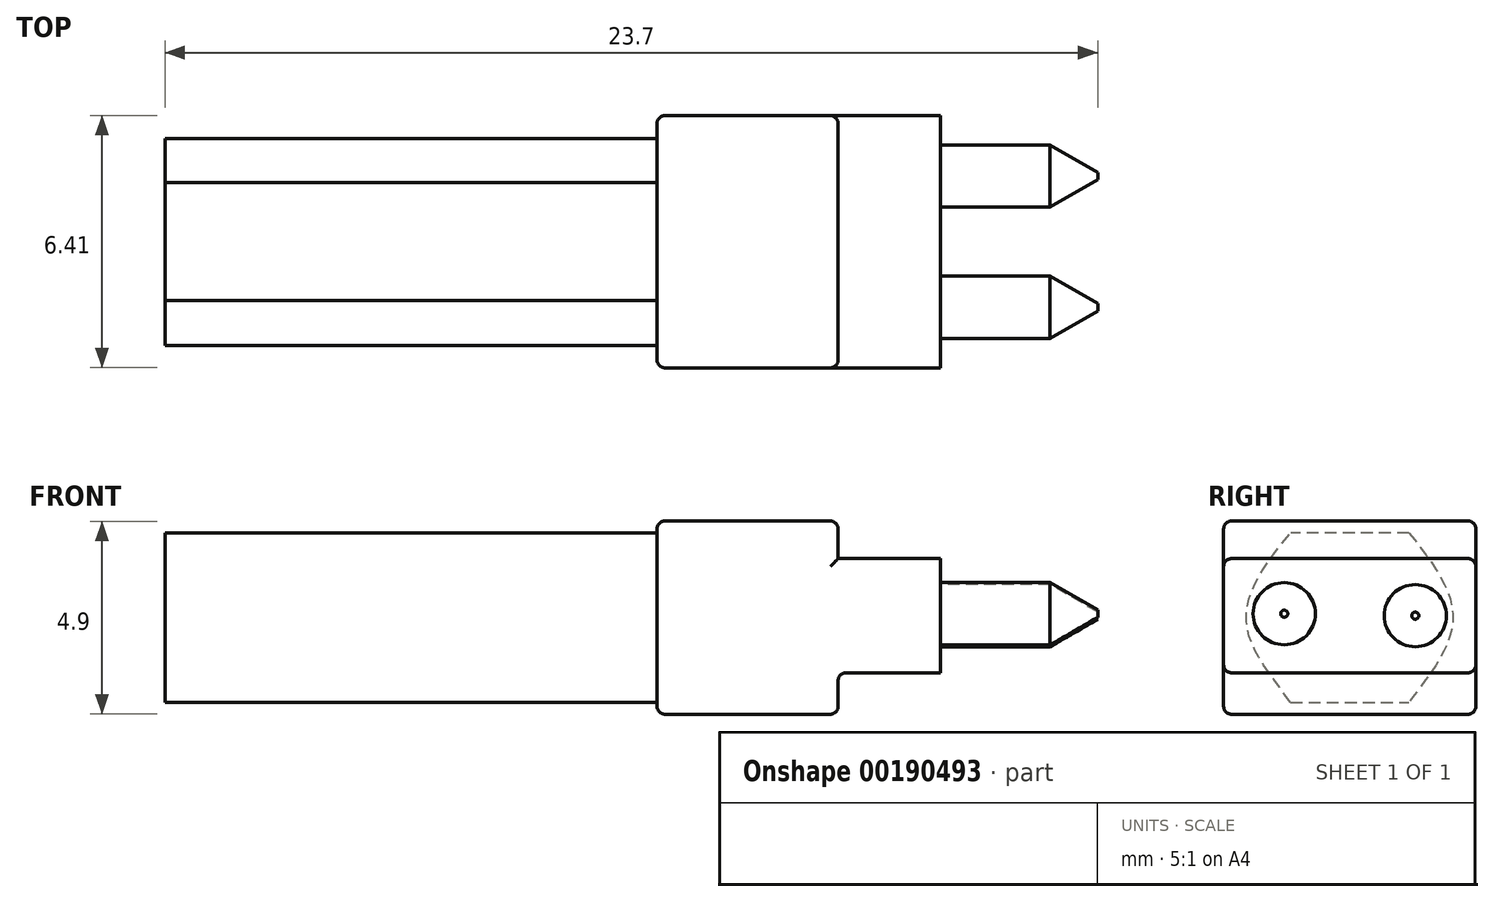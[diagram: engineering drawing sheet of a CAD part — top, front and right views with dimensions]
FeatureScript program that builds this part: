
annotation { "Feature Type Name" : "Feature", "Feature Type Description" : "" }
export const myFeature = defineFeature(function(context is Context, id is Id, definition is map)
    precondition{}
    {
        {
            var Q0;
            Q0=qCreatedBy(makeId("Top.planeOp"),FACE);
            var sketch = newSketch(context, id + "F0", { "sketchPlane" : qUnion([Q0])});
            skLineSegment(sketch, "E0.bottom", {"start": v(-2.48, 2.08) * mm, "end": v(4.72, 2.08) * mm});
            skLineSegment(sketch, "E0.top", {"start": v(-2.48, -4.33) * mm, "end": v(4.72, -4.33) * mm});
            skLineSegment(sketch, "E0.left", {"start": v(-2.48, 2.08) * mm, "end": v(-2.48, -4.33) * mm});
            skLineSegment(sketch, "E0.right", {"start": v(4.72, 2.08) * mm, "end": v(4.72, -4.33) * mm});
            skSolve(sketch);
        }
        {
            var Q0;
            Q0=makeQuery(id+"F0.imprint","IMPRINT",FACE,{"disambiguationData":[TD([[makeQuery(id+"F0.imprint","IMPRINT",EDGE,{"derivedFrom":sQuery(id+"F0.wireOp",EDGE,"E0.bottom")}),-1.0]])]});
            var sketch = newSketch(context, id + "F1", { "sketchPlane" : qUnion([Q0])});
            skSolve(sketch);
        }
        {
            var Q0;
            Q0=makeQuery(id+"F1.imprint","IMPRINT",FACE,{"disambiguationData":[TD([[makeQuery(id+"F1.imprint","IMPRINT",EDGE,{"derivedFrom":makeQuery(id+"F0.imprint","IMPRINT",EDGE,{"derivedFrom":sQuery(id+"F0.wireOp",EDGE,"E0.bottom")})}),-1.0]])]});
            extrude(context, id + "F2", {"entities" : qUnion([Q0]), "depth" : 2.9 * mm, "offsetDistance" : 25 * mm});
        }
        {
            var Q0;
            Q0=makeQuery(id+"F2.opExtrude","CAP_FACE",FACE,{"disambiguationData":[OSD([sQuery(id+"F0.wireOp",EDGE,"E0.bottom"),sQuery(id+"F0.wireOp",EDGE,"E0.top"),sQuery(id+"F0.wireOp",EDGE,"E0.left"),sQuery(id+"F0.wireOp",EDGE,"E0.right")])],"isStart":false});
            var sketch = newSketch(context, id + "F3", { "sketchPlane" : qUnion([Q0])});
            skLineSegment(sketch, "E1.bottom", {"start": v(-2.48, 2.08) * mm, "end": v(2.12, 2.08) * mm});
            skLineSegment(sketch, "E1.top", {"start": v(-2.48, -4.33) * mm, "end": v(2.12, -4.33) * mm});
            skLineSegment(sketch, "E1.left", {"start": v(-2.48, 2.08) * mm, "end": v(-2.48, -4.33) * mm});
            skLineSegment(sketch, "E1.right", {"start": v(2.12, 2.08) * mm, "end": v(2.12, -4.33) * mm});
            skSolve(sketch);
        }
        {
            var Q0;
            Q0 = qSketchRegion(id + "F3", true);
            extrude(context, id + "F4", {"entities" : qUnion([Q0]), "operationType" : NewBodyOperationType.ADD, "depth" : 0.95 * mm, "offsetDistance" : 25 * mm});
        }
        {
            var Q0;
            Q0 = qSketchRegion(id + "F3", true);
            extrude(context, id + "F5", {"entities" : qUnion([Q0]), "operationType" : NewBodyOperationType.ADD, "oppositeDirection" : true, "depth" : 3.96 * mm, "offsetDistance" : 25 * mm});
        }
        {
            var Q0;
            Q0=makeQuery(id+"F4.opExtrude","CAP_EDGE",EDGE,{"disambiguationData":[OSD([sQuery(id+"F3.wireOp",EDGE,"E1.right")])],"isStart":false});
            var Q1;
            Q1=makeQuery(id+"F4.opExtrude","CAP_EDGE",EDGE,{"disambiguationData":[OSD([sQuery(id+"F3.wireOp",EDGE,"E1.top")])],"isStart":false});
            var Q2;
            Q2=makeQuery(id+"F4.opExtrude","CAP_EDGE",EDGE,{"disambiguationData":[OSD([sQuery(id+"F3.wireOp",EDGE,"E1.left")])],"isStart":false});
            var Q3;
            Q3=makeQuery(id+"F4.opExtrude","CAP_EDGE",EDGE,{"disambiguationData":[OSD([sQuery(id+"F3.wireOp",EDGE,"E1.bottom")])],"isStart":false});
            var Q4;
            Q4=makeQuery(id+"F2.opExtrude","CAP_EDGE",EDGE,{"disambiguationData":[OSD([sQuery(id+"F0.wireOp",EDGE,"E0.top")])],"isStart":false});
            var Q5;
            Q5=makeQuery(id+"F4.opExtrude","SWEPT_EDGE",EDGE,{"disambiguationData":[OSD([sQuery(id+"F0.wireOp",EDGE,"E0.top"),sQuery(id+"F3.wireOp",EDGE,"E1.top"),sQuery(id+"F3.wireOp",EDGE,"E1.right")])]});
            var Q6;
            {var subQ0=sQuery(id+"F3.wireOp",EDGE,"E1.left");var subQ1=sQuery(id+"F3.wireOp",EDGE,"E1.top");Q6=makeQuery(id+"F5.boolean.opBoolean","MERGE",EDGE,{"derivedFrom":[makeQuery(id+"F4.boolean.opBoolean","MERGE",EDGE,{"derivedFrom":[makeQuery(id+"F2.opExtrude","SWEPT_EDGE",EDGE,{"disambiguationData":[OSD([sQuery(id+"F0.wireOp",EDGE,"E0.top"),sQuery(id+"F0.wireOp",EDGE,"E0.left")])]}),makeQuery(id+"F4.opExtrude","SWEPT_EDGE",EDGE,{"disambiguationData":[OSD([subQ1,subQ0])]})]}),makeQuery(id+"F5.opExtrude","SWEPT_EDGE",EDGE,{"disambiguationData":[OSD([subQ1,subQ0])]})]});}
            var Q7;
            Q7=makeQuery(id+"F5.opExtrude","CAP_EDGE",EDGE,{"disambiguationData":[OSD([sQuery(id+"F3.wireOp",EDGE,"E1.top")])],"isStart":false});
            var Q8;
            Q8=makeQuery(id+"F5.opExtrude","CAP_EDGE",EDGE,{"disambiguationData":[OSD([sQuery(id+"F3.wireOp",EDGE,"E1.right")])],"isStart":false});
            var Q9;
            Q9=makeQuery(id+"F5.opExtrude","CAP_EDGE",EDGE,{"disambiguationData":[OSD([sQuery(id+"F3.wireOp",EDGE,"E1.bottom")])],"isStart":false});
            var Q10;
            Q10=makeQuery(id+"F5.opExtrude","SWEPT_EDGE",EDGE,{"disambiguationData":[OSD([sQuery(id+"F0.wireOp",EDGE,"E0.top"),sQuery(id+"F3.wireOp",EDGE,"E1.top"),sQuery(id+"F3.wireOp",EDGE,"E1.right")])]});
            var Q11;
            Q11=makeQuery(id+"F2.opExtrude","CAP_EDGE",EDGE,{"disambiguationData":[OSD([sQuery(id+"F0.wireOp",EDGE,"E0.top")])],"isStart":true});
            var Q12;
            Q12=makeQuery(id+"F5.opExtrude","SWEPT_EDGE",EDGE,{"disambiguationData":[OSD([sQuery(id+"F0.wireOp",EDGE,"E0.bottom"),sQuery(id+"F3.wireOp",EDGE,"E1.bottom"),sQuery(id+"F3.wireOp",EDGE,"E1.right")])]});
            var Q13;
            Q13=makeQuery(id+"F2.opExtrude","CAP_EDGE",EDGE,{"disambiguationData":[OSD([sQuery(id+"F0.wireOp",EDGE,"E0.bottom")])],"isStart":false});
            var Q14;
            Q14=makeQuery(id+"F4.opExtrude","SWEPT_EDGE",EDGE,{"disambiguationData":[OSD([sQuery(id+"F0.wireOp",EDGE,"E0.bottom"),sQuery(id+"F3.wireOp",EDGE,"E1.bottom"),sQuery(id+"F3.wireOp",EDGE,"E1.right")])]});
            var Q15;
            Q15=makeQuery(id+"F2.opExtrude","CAP_EDGE",EDGE,{"disambiguationData":[OSD([sQuery(id+"F0.wireOp",EDGE,"E0.bottom")])],"isStart":true});
            var Q16;
            {var subQ0=sQuery(id+"F3.wireOp",EDGE,"E1.left");var subQ1=sQuery(id+"F3.wireOp",EDGE,"E1.bottom");Q16=makeQuery(id+"F5.boolean.opBoolean","MERGE",EDGE,{"derivedFrom":[makeQuery(id+"F4.boolean.opBoolean","MERGE",EDGE,{"derivedFrom":[makeQuery(id+"F2.opExtrude","SWEPT_EDGE",EDGE,{"disambiguationData":[OSD([sQuery(id+"F0.wireOp",EDGE,"E0.bottom"),sQuery(id+"F0.wireOp",EDGE,"E0.left")])]}),makeQuery(id+"F4.opExtrude","SWEPT_EDGE",EDGE,{"disambiguationData":[OSD([subQ1,subQ0])]})]}),makeQuery(id+"F5.opExtrude","SWEPT_EDGE",EDGE,{"disambiguationData":[OSD([subQ1,subQ0])]})]});}
            var Q17;
            Q17=makeQuery(id+"F5.opExtrude","CAP_EDGE",EDGE,{"disambiguationData":[OSD([sQuery(id+"F3.wireOp",EDGE,"E1.left")])],"isStart":false});
            var Q18;
            Q18=makeQuery(id+"F5.boolean.opBoolean","INTERSECT",EDGE,{"derivedFrom":[makeQuery(id+"F2.opExtrude","CAP_FACE",FACE,{"disambiguationData":[OSD([sQuery(id+"F0.wireOp",EDGE,"E0.bottom"),sQuery(id+"F0.wireOp",EDGE,"E0.top"),sQuery(id+"F0.wireOp",EDGE,"E0.left"),sQuery(id+"F0.wireOp",EDGE,"E0.right")])],"isStart":true}),makeQuery(id+"F5.opExtrude","SWEPT_FACE",FACE,{"disambiguationData":[OSD([sQuery(id+"F3.wireOp",EDGE,"E1.right")])]})]});
            fillet(context, id + "F6", {"entities" : qUnion([Q0, Q1, Q2, Q3, Q4, Q5, Q6, Q7, Q8, Q9, Q10, Q11, Q12, Q13, Q14, Q15, Q16, Q17, Q18]), "tangentPropagation" : true, "radius" : .2 * mm, "defaultsChanged" : false, "vertexSettings" : [], "allowEdgeOverflow" : false});
        }
        {
            var Q0;
            Q0=makeQuery(id+"F2.opExtrude","SWEPT_FACE",FACE,{"disambiguationData":[OSD([sQuery(id+"F0.wireOp",EDGE,"E0.right")])]});
            var sketch = newSketch(context, id + "F7", { "sketchPlane" : qUnion([Q0])});
            skCircle(sketch, "E2", {"center": v(-2.8, 1.5) * mm, "radius": 0.79 * mm});
            skCircle(sketch, "E3", {"center": v(0.54, 1.45) * mm, "radius": 0.79 * mm});
            skSolve(sketch);
        }
        {
            var Q0;
            Q0 = qSketchRegion(id + "F7", true);
            var Q1;
            Q1 = qSketchRegion(id + "FXM3ZPi4sPy6rrn_1", true);
            extrude(context, id + "F8", {"entities" : qUnion([Q0, Q1]), "operationType" : NewBodyOperationType.ADD, "depth" : 4 * mm, "offsetDistance" : 25 * mm});
        }
        {
            var Q0;
            Q0=makeQuery(id+"F8.opExtrude","CAP_FACE",FACE,{"disambiguationData":[OSD([sQuery(id+"F7.wireOp",EDGE,"E2")])],"isStart":false});
            var Q1;
            Q1=makeQuery(id+"F8.opExtrude","CAP_FACE",FACE,{"disambiguationData":[OSD([sQuery(id+"F7.wireOp",EDGE,"E3")])],"isStart":false});
            chamfer(context, id + "F9", {"entities" : qUnion([Q0, Q1]), "chamferType" : ChamferType.OFFSET_ANGLE, "width" : .7 * mm, "oppositeDirection" : false, "angle" : 60 * degree, "tangentPropagation" : true});
        }
        {
            var Q0;
            {var subQ0=sQuery(id+"F3.wireOp",EDGE,"E1.left");Q0=makeQuery(id+"F5.boolean.opBoolean","MERGE",FACE,{"derivedFrom":[makeQuery(id+"F4.boolean.opBoolean","MERGE",FACE,{"derivedFrom":[makeQuery(id+"F2.opExtrude","SWEPT_FACE",FACE,{"disambiguationData":[OSD([sQuery(id+"F0.wireOp",EDGE,"E0.left")])]}),makeQuery(id+"F4.opExtrude","SWEPT_FACE",FACE,{"disambiguationData":[OSD([subQ0])]})]}),makeQuery(id+"F5.opExtrude","SWEPT_FACE",FACE,{"disambiguationData":[OSD([subQ0])]})]});}
            var sketch = newSketch(context, id + "F10", { "sketchPlane" : qUnion([Q0])});
            skLineSegment(sketch, "E4", {"start": v(-0.38, 3.56) * mm, "end": v(2.62, 3.56) * mm});
            skLineSegment(sketch, "E5", {"start": v(2.63, -0.76) * mm, "end": v(-0.37, -0.76) * mm});
            skFitSpline(sketch, "E6", {"points": [v(-0.38, 3.55) * mm, v(-1.5, 1.4) * mm, v(-0.37, -0.76) * mm], "startDerivative": vector(-3.36, -4.25) * mm, "endDerivative": vector(3.37, -4.37) * mm});
            skFitSpline(sketch, "E7", {"points": [v(2.63, -0.76) * mm, v(3.76, 1.4) * mm, v(2.62, 3.56) * mm], "startDerivative": vector(3.34, 4.59) * mm, "endDerivative": vector(-3.42, 4.03) * mm});
            skSolve(sketch);
        }
        {
            var Q0;
            Q0 = qSketchRegion(id + "F10", true);
            extrude(context, id + "F11", {"entities" : qUnion([Q0]), "operationType" : NewBodyOperationType.ADD, "depth" : 12.5 * mm, "offsetDistance" : 25 * mm});
        }
    });
